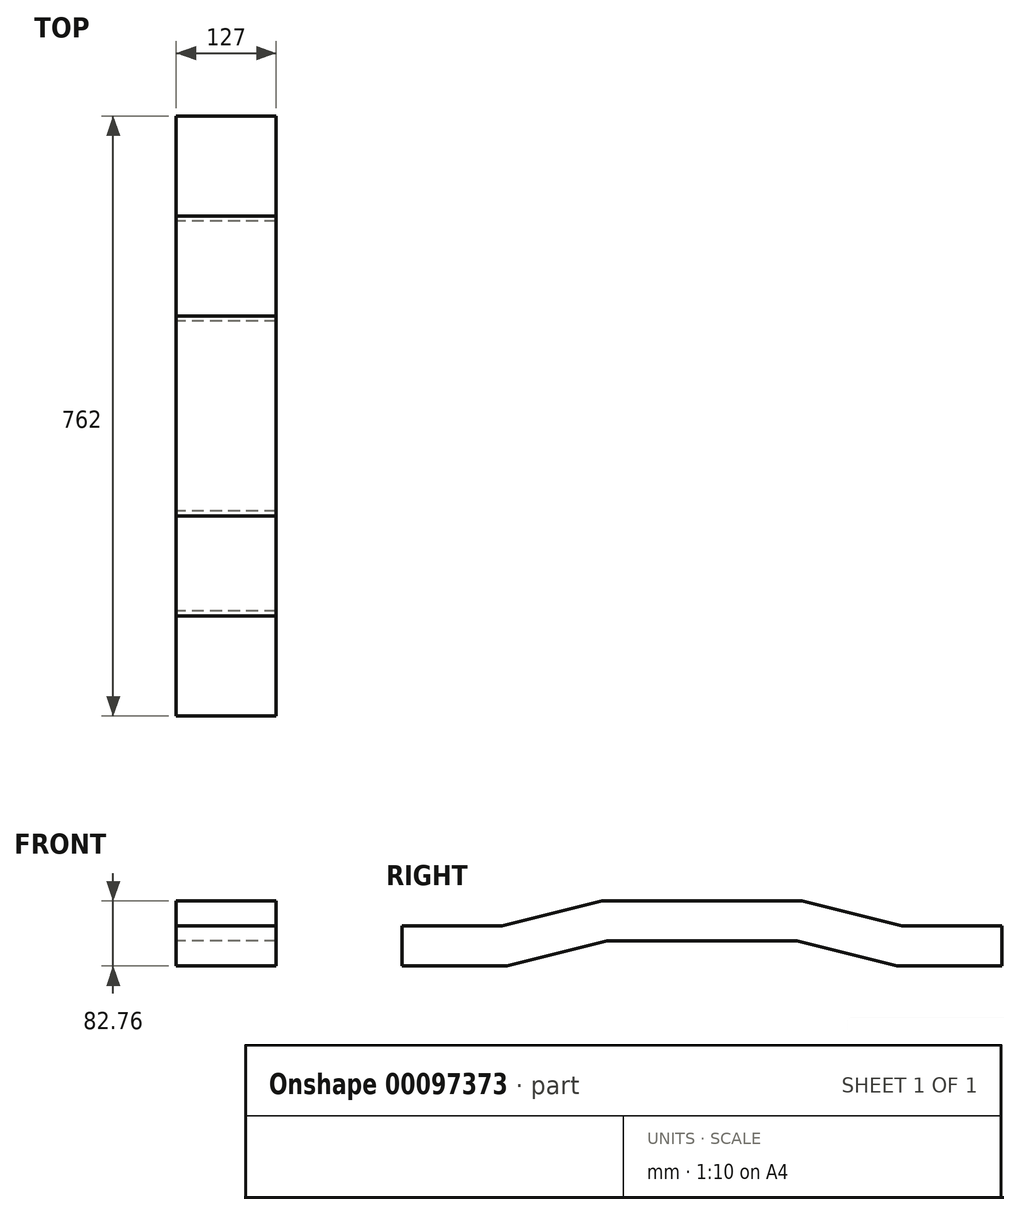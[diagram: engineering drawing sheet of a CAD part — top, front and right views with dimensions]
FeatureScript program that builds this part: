
annotation { "Feature Type Name" : "Feature", "Feature Type Description" : "" }
export const myFeature = defineFeature(function(context is Context, id is Id, definition is map)
    precondition{}
    {
        {
            var Q0;
            Q0=qCreatedBy(makeId("Right.planeOp"),FACE);
            var sketch = newSketch(context, id + "F0", { "sketchPlane" : qUnion([Q0])});
            skLineSegment(sketch, "E0", {"start": v(127, 0) * mm, "end": v(0, 0) * mm});
            skPoint(sketch, "E1", {"position": v(0, 0) * mm});
            skLineSegment(sketch, "E2", {"start": v(381, -31.96) * mm, "end": v(254, -31.96) * mm});
            skLineSegment(sketch, "E3", {"start": v(254, -31.96) * mm, "end": v(127, 0) * mm});
            skLineSegment(sketch, "E4.0", {"start": v(120.7, -50.8) * mm, "end": v(0, -50.8) * mm});
            skLineSegment(sketch, "E4.1", {"start": v(247.7, -82.76) * mm, "end": v(120.7, -50.8) * mm});
            skLineSegment(sketch, "E4.2", {"start": v(381, -82.76) * mm, "end": v(247.7, -82.76) * mm});
            skLineSegment(sketch, "E5", {"start": v(381, -31.96) * mm, "end": v(381, -82.76) * mm});
            skLineSegment(sketch, "E6", {"start": v(0, 0) * mm, "end": v(0, -50.8) * mm, "construction": true});
            skLineSegment(sketch, "E7.MirrorCS", {"start": v(-381, -31.96) * mm, "end": v(-254, -31.96) * mm});
            skLineSegment(sketch, "E8.MirrorCS", {"start": v(-127, 0) * mm, "end": v(0, 0) * mm});
            skLineSegment(sketch, "E9.MirrorCS", {"start": v(-247.7, -82.76) * mm, "end": v(-120.7, -50.8) * mm});
            skLineSegment(sketch, "E10.MirrorCS", {"start": v(-120.7, -50.8) * mm, "end": v(0, -50.8) * mm});
            skLineSegment(sketch, "E11.MirrorCS", {"start": v(-254, -31.96) * mm, "end": v(-127, 0) * mm});
            skLineSegment(sketch, "E12.MirrorCS", {"start": v(-381, -31.96) * mm, "end": v(-381, -82.76) * mm});
            skLineSegment(sketch, "E13.MirrorCS", {"start": v(-381, -82.76) * mm, "end": v(-247.7, -82.76) * mm});
            skSolve(sketch);
        }
        {
            var Q0;
            Q0 = qSketchRegion(id + "F0", true);
            extrude(context, id + "F1", {"entities" : qUnion([Q0]), "depth" : 127 * mm});
        }
    });
